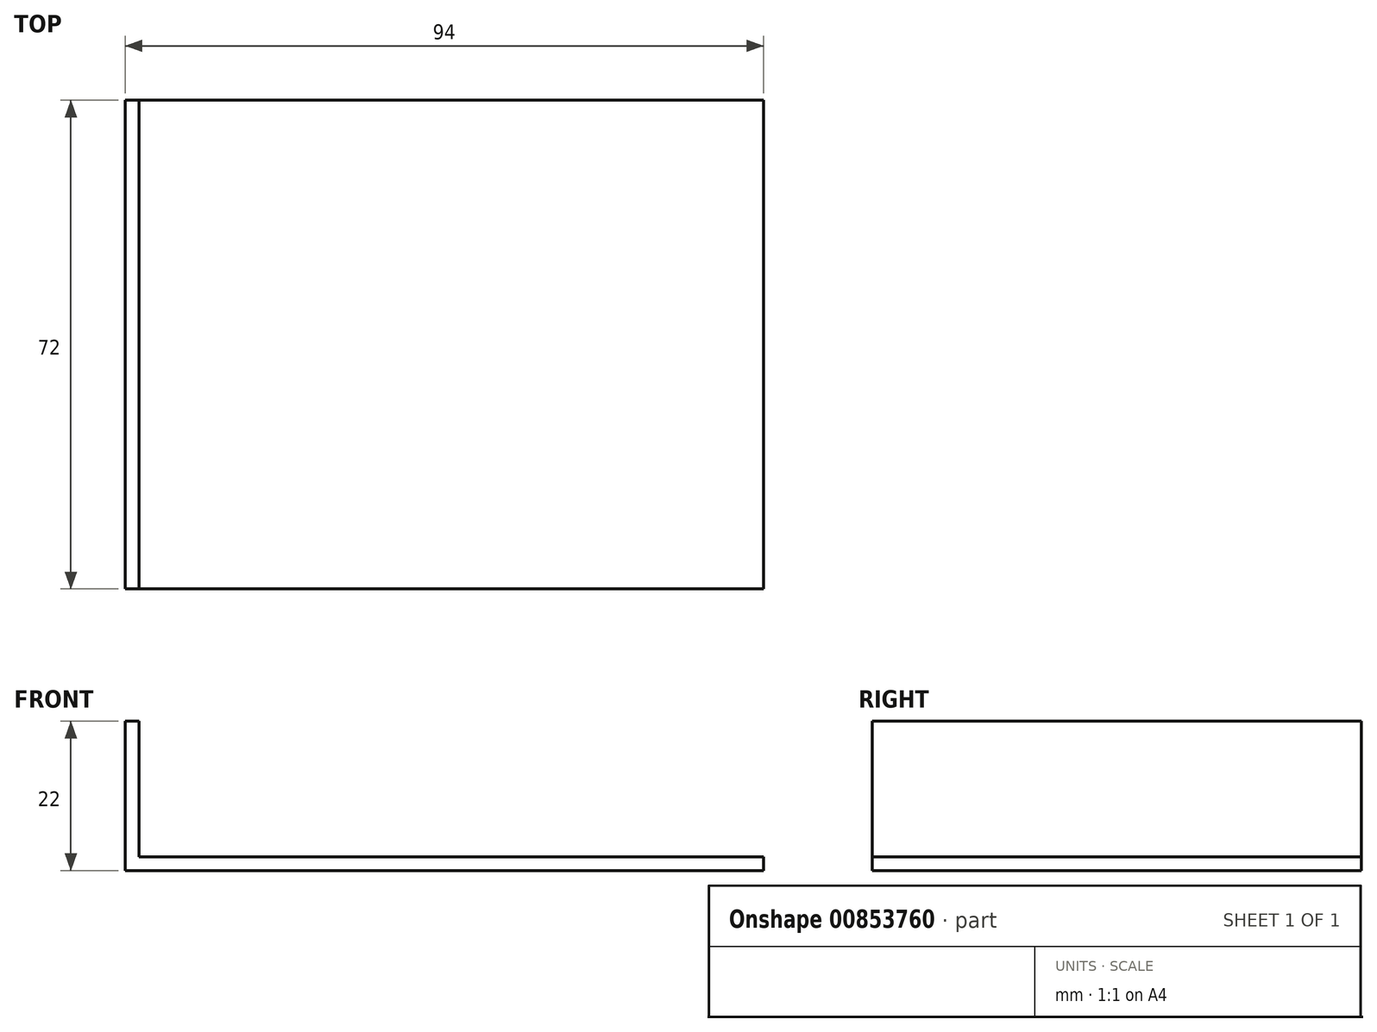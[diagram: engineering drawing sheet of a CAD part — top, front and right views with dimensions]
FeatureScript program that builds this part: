
annotation { "Feature Type Name" : "Feature", "Feature Type Description" : "" }
export const myFeature = defineFeature(function(context is Context, id is Id, definition is map)
    precondition{}
    {
        {
            var Q0;
            Q0=qCreatedBy(makeId("Top.planeOp"),FACE);
            var sketch = newSketch(context, id + "F0", { "sketchPlane" : qUnion([Q0])});
            skLineSegment(sketch, "E0.bottom", {"start": v(47, 36) * mm, "end": v(-47, 36) * mm});
            skLineSegment(sketch, "E0.top", {"start": v(47, -36) * mm, "end": v(-47, -36) * mm});
            skLineSegment(sketch, "E0.left", {"start": v(47, 36) * mm, "end": v(47, -36) * mm});
            skLineSegment(sketch, "E0.right", {"start": v(-47, 36) * mm, "end": v(-47, -36) * mm});
            skPoint(sketch, "E0.middle", {"position": v(0, 0) * mm});
            skSolve(sketch);
        }
        {
            var Q0;
            Q0 = qSketchRegion(id + "F0", true);
            extrude(context, id + "F1", {"entities" : qUnion([Q0]), "depth" : 2 * mm, "offsetDistance" : 25 * mm});
        }
        {
            var Q0;
            Q0=qCreatedBy(makeId("Front.planeOp"),FACE);
            var sketch = newSketch(context, id + "F2", { "sketchPlane" : qUnion([Q0])});
            skLineSegment(sketch, "E1.bottom", {"start": v(-47, 0) * mm, "end": v(-45, 0) * mm});
            skLineSegment(sketch, "E1.top", {"start": v(-47, 22) * mm, "end": v(-45, 22) * mm});
            skLineSegment(sketch, "E1.left", {"start": v(-47, 0) * mm, "end": v(-47, 22) * mm});
            skLineSegment(sketch, "E1.right", {"start": v(-45, 0) * mm, "end": v(-45, 22) * mm});
            skLineSegment(sketch, "E2", {"start": v(-45, 22) * mm, "end": v(47.59, 22) * mm});
            skSolve(sketch);
        }
        {
            var Q0;
            Q0 = qSketchRegion(id + "F2", true);
            extrude(context, id + "F3", {"entities" : qUnion([Q0]), "operationType" : NewBodyOperationType.ADD, "endBound" : BoundingType.SYMMETRIC, "depth" : 72 * mm, "offsetDistance" : 25 * mm});
        }
    });
